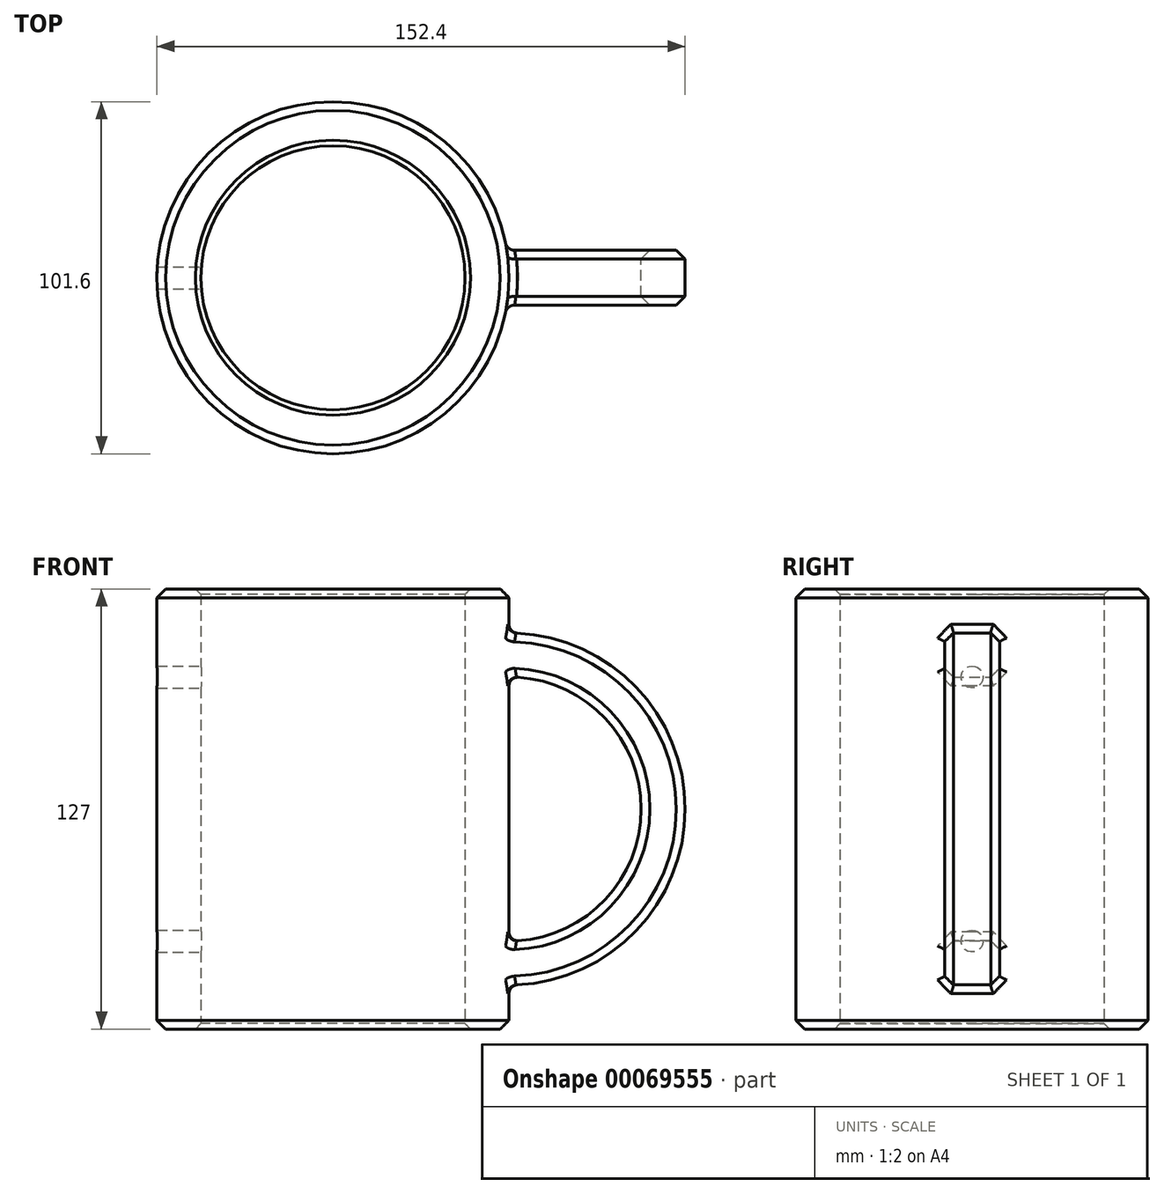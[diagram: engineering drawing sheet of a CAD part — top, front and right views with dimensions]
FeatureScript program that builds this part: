
annotation { "Feature Type Name" : "Feature", "Feature Type Description" : "" }
export const myFeature = defineFeature(function(context is Context, id is Id, definition is map)
    precondition{}
    {
        {
            var Q0;
            Q0=qCreatedBy(makeId("Top.planeOp"),FACE);
            var sketch = newSketch(context, id + "F0", { "sketchPlane" : qUnion([Q0])});
            skCircle(sketch, "E0", {"center": v(0, 0) * mm, "radius": 38.1 * mm});
            skCircle(sketch, "E1", {"center": v(0, 0) * mm, "radius": 50.8 * mm});
            skSolve(sketch);
        }
        {
            var Q0;
            Q0 = qSketchRegion(id + "F0", true);
            extrude(context, id + "F1", {"entities" : qUnion([Q0]), "depth" : 63.5 * mm});
        }
        {
            var Q0;
            Q0=qCreatedBy(makeId("Top.planeOp"),FACE);
            var sketch = newSketch(context, id + "F2", { "sketchPlane" : qUnion([Q0])});
            skLineSegment(sketch, "E2.rect.bottom", {"start": v(88.9, 7.94) * mm, "end": v(101.6, 7.94) * mm});
            skLineSegment(sketch, "E2.rect.top", {"start": v(88.9, -7.94) * mm, "end": v(101.6, -7.94) * mm});
            skLineSegment(sketch, "E2.rect.left", {"start": v(88.9, 7.94) * mm, "end": v(88.9, -7.94) * mm});
            skLineSegment(sketch, "E2.rect.right", {"start": v(101.6, 7.94) * mm, "end": v(101.6, -7.94) * mm});
            skPoint(sketch, "E2.rect.middle", {"position": v(95.25, 0) * mm});
            skLineSegment(sketch, "E3", {"start": v(95.25, 0) * mm, "end": v(50.8, 0) * mm, "construction": true});
            skLineSegment(sketch, "E4", {"start": v(50.8, 0) * mm, "end": v(50.8, 61.95) * mm, "construction": true});
            skSolve(sketch);
        }
        {
            var Q0;
            Q0=makeQuery(id+"F2.imprint","IMPRINT",FACE,{"disambiguationData":[TD([[makeQuery(id+"F2.imprint","IMPRINT",EDGE,{"derivedFrom":sQuery(id+"F2.wireOp",EDGE,"E2.rect.bottom")}),-1.0]])]});
            var Q1;
            Q1 = qConstructionFilter(qBodyType(qCreatedBy(id + "F2" ,EDGE), BodyType.WIRE), ConstructionObject.NO);
            var Q2;
            Q2=sQuery(id+"F2.wireOp",EDGE,"E4");
            revolve(context, id + "F3", {"operationType" : NewBodyOperationType.ADD, "entities" : qUnion([Q0]), "surfaceEntities" : qUnion([Q1]), "axis" : qUnion([Q2]), "revolveType" : RevolveType.ONE_DIRECTION, "oppositeDirection" : true, "angle" : 100 * degree});
        }
        {
            var Q0;
            Q0=makeQuery(id+"F3.opRevolve","SWEPT_EDGE",EDGE,{"disambiguationData":[OSD([sQuery(id+"F2.wireOp",EDGE,"E2.rect.top"),sQuery(id+"F2.wireOp",EDGE,"E2.rect.right")])]});
            var Q1;
            Q1=makeQuery(id+"F3.opRevolve","SWEPT_EDGE",EDGE,{"disambiguationData":[OSD([sQuery(id+"F2.wireOp",EDGE,"E2.rect.top"),sQuery(id+"F2.wireOp",EDGE,"E2.rect.left")])]});
            var Q2;
            Q2=makeQuery(id+"F3.opRevolve","SWEPT_EDGE",EDGE,{"disambiguationData":[OSD([sQuery(id+"F2.wireOp",EDGE,"E2.rect.bottom"),sQuery(id+"F2.wireOp",EDGE,"E2.rect.right")])]});
            var Q3;
            Q3=makeQuery(id+"F3.opRevolve","SWEPT_EDGE",EDGE,{"disambiguationData":[OSD([sQuery(id+"F2.wireOp",EDGE,"E2.rect.bottom"),sQuery(id+"F2.wireOp",EDGE,"E2.rect.left")])]});
            var Q4;
            Q4=makeQuery(id+"F1.opExtrude","CAP_EDGE",EDGE,{"disambiguationData":[OSD([sQuery(id+"F0.wireOp",EDGE,"E1")])],"isStart":false});
            chamfer(context, id + "F4", {"entities" : qUnion([Q0, Q1, Q2, Q3, Q4]), "width" : 2.54 * mm, "tangentPropagation" : true});
        }
        {
            var Q0;
            Q0=makeQuery(id+"F1.opExtrude","CAP_EDGE",EDGE,{"disambiguationData":[OSD([sQuery(id+"F0.wireOp",EDGE,"E0")])],"isStart":false});
            chamfer(context, id + "F5", {"entities" : qUnion([Q0]), "width" : 1.57 * mm, "tangentPropagation" : true});
        }
        {
            var Q0;
            Q0=makeQuery(id+"F3.boolean.opBoolean","INTERSECT",EDGE,{"derivedFrom":[makeQuery(id+"F1.opExtrude","SWEPT_FACE",FACE,{"disambiguationData":[OSD([sQuery(id+"F0.wireOp",EDGE,"E1")])]}),makeQuery(id+"F3.opRevolve","SWEPT_FACE",FACE,{"disambiguationData":[OSD([sQuery(id+"F2.wireOp",EDGE,"E2.rect.right")])]})]});
            var Q1;
            Q1=makeQuery(id+"F4.opChamfer","BLEND_EDGE",EDGE,{"blendedFrom":[makeQuery(id+"F3.opRevolve","SWEPT_EDGE",EDGE,{"disambiguationData":[OSD([sQuery(id+"F2.wireOp",EDGE,"E2.rect.bottom"),sQuery(id+"F2.wireOp",EDGE,"E2.rect.right")])]}),makeQuery(id+"F1.opExtrude","SWEPT_FACE",FACE,{"disambiguationData":[OSD([sQuery(id+"F0.wireOp",EDGE,"E1")])]})],"blendedInto":[makeQuery(id+"F1.opExtrude","SWEPT_FACE",FACE,{"disambiguationData":[OSD([sQuery(id+"F0.wireOp",EDGE,"E1")])]})]});
            var Q2;
            Q2=makeQuery(id+"F3.boolean.opBoolean","INTERSECT",EDGE,{"derivedFrom":[makeQuery(id+"F1.opExtrude","SWEPT_FACE",FACE,{"disambiguationData":[OSD([sQuery(id+"F0.wireOp",EDGE,"E1")])]}),makeQuery(id+"F3.opRevolve","SWEPT_FACE",FACE,{"disambiguationData":[OSD([sQuery(id+"F2.wireOp",EDGE,"E2.rect.bottom")])]})]});
            var Q3;
            Q3=makeQuery(id+"F4.opChamfer","BLEND_EDGE",EDGE,{"blendedFrom":[makeQuery(id+"F3.opRevolve","SWEPT_EDGE",EDGE,{"disambiguationData":[OSD([sQuery(id+"F2.wireOp",EDGE,"E2.rect.top"),sQuery(id+"F2.wireOp",EDGE,"E2.rect.right")])]}),makeQuery(id+"F1.opExtrude","SWEPT_FACE",FACE,{"disambiguationData":[OSD([sQuery(id+"F0.wireOp",EDGE,"E1")])]})],"blendedInto":[makeQuery(id+"F1.opExtrude","SWEPT_FACE",FACE,{"disambiguationData":[OSD([sQuery(id+"F0.wireOp",EDGE,"E1")])]})]});
            var Q4;
            Q4=makeQuery(id+"F3.boolean.opBoolean","INTERSECT",EDGE,{"derivedFrom":[makeQuery(id+"F1.opExtrude","SWEPT_FACE",FACE,{"disambiguationData":[OSD([sQuery(id+"F0.wireOp",EDGE,"E1")])]}),makeQuery(id+"F3.opRevolve","SWEPT_FACE",FACE,{"disambiguationData":[OSD([sQuery(id+"F2.wireOp",EDGE,"E2.rect.top")])]})]});
            var Q5;
            Q5=makeQuery(id+"F4.opChamfer","BLEND_EDGE",EDGE,{"blendedFrom":[makeQuery(id+"F3.opRevolve","SWEPT_EDGE",EDGE,{"disambiguationData":[OSD([sQuery(id+"F2.wireOp",EDGE,"E2.rect.top"),sQuery(id+"F2.wireOp",EDGE,"E2.rect.left")])]}),makeQuery(id+"F1.opExtrude","SWEPT_FACE",FACE,{"disambiguationData":[OSD([sQuery(id+"F0.wireOp",EDGE,"E1")])]})],"blendedInto":[makeQuery(id+"F1.opExtrude","SWEPT_FACE",FACE,{"disambiguationData":[OSD([sQuery(id+"F0.wireOp",EDGE,"E1")])]})]});
            var Q6;
            Q6=makeQuery(id+"F3.boolean.opBoolean","INTERSECT",EDGE,{"derivedFrom":[makeQuery(id+"F1.opExtrude","SWEPT_FACE",FACE,{"disambiguationData":[OSD([sQuery(id+"F0.wireOp",EDGE,"E1")])]}),makeQuery(id+"F3.opRevolve","SWEPT_FACE",FACE,{"disambiguationData":[OSD([sQuery(id+"F2.wireOp",EDGE,"E2.rect.left")])]})]});
            var Q7;
            Q7=makeQuery(id+"F4.opChamfer","BLEND_EDGE",EDGE,{"blendedFrom":[makeQuery(id+"F3.opRevolve","SWEPT_EDGE",EDGE,{"disambiguationData":[OSD([sQuery(id+"F2.wireOp",EDGE,"E2.rect.bottom"),sQuery(id+"F2.wireOp",EDGE,"E2.rect.left")])]}),makeQuery(id+"F1.opExtrude","SWEPT_FACE",FACE,{"disambiguationData":[OSD([sQuery(id+"F0.wireOp",EDGE,"E1")])]})],"blendedInto":[makeQuery(id+"F1.opExtrude","SWEPT_FACE",FACE,{"disambiguationData":[OSD([sQuery(id+"F0.wireOp",EDGE,"E1")])]})]});
            fillet(context, id + "F6", {"entities" : qUnion([Q0, Q1, Q2, Q3, Q4, Q5, Q6, Q7]), "radius" : 2.54 * mm, "tangentPropagation" : true, "allowEdgeOverflow" : false});
        }
        {
            var Q0;
            Q0=makeQuery(id+"F1.opExtrude","SWEPT_BODY",BODY,{"disambiguationData":[OSD([sQuery(id+"F0.wireOp",EDGE,"E0"),sQuery(id+"F0.wireOp",EDGE,"E1")])]});
            var Q1;
            Q1=qCreatedBy(makeId("Top.planeOp"),FACE);
            mirror(context, id + "F7", {"operationType" : NewBodyOperationType.ADD, "entities" : qUnion([Q0]), "mirrorPlane" : qUnion([Q1])});
        }
        {
            var Q0;
            Q0=qCreatedBy(makeId("Right.planeOp"),FACE);
            var sketch = newSketch(context, id + "F8", { "sketchPlane" : qUnion([Q0])});
            skLineSegment(sketch, "E5", {"start": v(0, 38.1) * mm, "end": v(0, -38.1) * mm});
            skSolve(sketch);
        }
        {
            var Q0;
            Q0=sQuery(id+"F8.wireOp",VERTEX,"E5.start");
            var Q1;
            Q1=sQuery(id+"F8.wireOp",VERTEX,"E5.end");
            var Q2;
            Q2=makeQuery(id+"F1.opExtrude","SWEPT_BODY",BODY,{"disambiguationData":[OSD([sQuery(id+"F0.wireOp",EDGE,"E0"),sQuery(id+"F0.wireOp",EDGE,"E1")])]});
            hole(context, id + "F9", {"style" : HoleStyle.SIMPLE, "holeDiameter" : 6.35 * mm, "endStyle" : HoleEndStyle.THROUGH, "locations" : qUnion([Q0, Q1]), "scope" : qUnion([Q2])});
        }
    });
